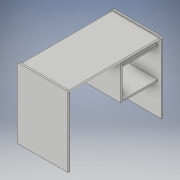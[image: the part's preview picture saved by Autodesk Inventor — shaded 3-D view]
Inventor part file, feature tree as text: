
AUTODESK INVENTOR PART (.ipt)
format: ipt  version: 2017 (Build 210142000, 142)  size: 187,392 bytes
history: native  units: in
note: dims shown in document units (in); Inventor stores cm internally (conversion verified against a paired STEP export)
features: other x3, extrude x1, sketch x1
ambient origin geometry x8: Origin, YZ Plane, XZ Plane, XY Plane, X Axis, Y Axis, Z Axis, Center Point
bodies: Solid1 (feature_tree)
feature tree (5):
  other  "table.ipt"
  extrude  "Extrusion1"  Depth=0.0328in TaperAngle=0.0deg
  other  "Solid1::table.ipt"
  other  "TaggingFeature1"
  sketch  "Sketch1"  dims[d0=0.0328in d1=1.5in d2=0.0in]
